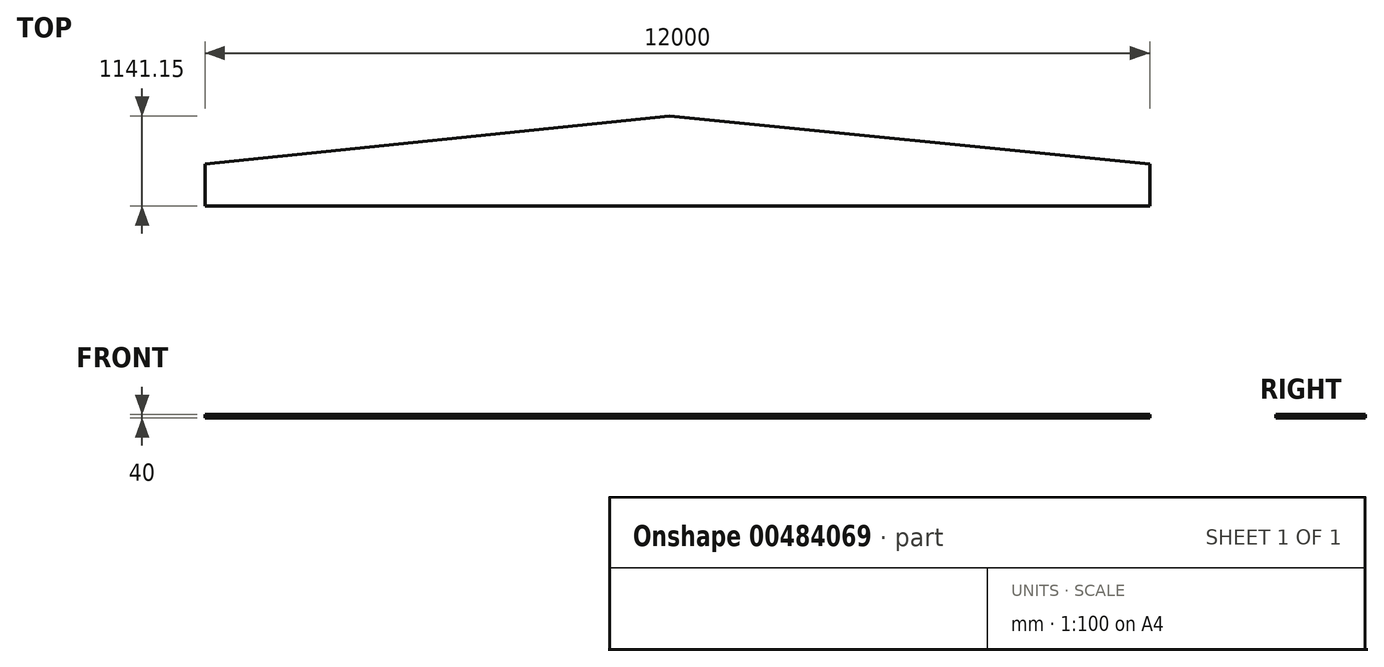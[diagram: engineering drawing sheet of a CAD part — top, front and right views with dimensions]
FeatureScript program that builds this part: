
annotation { "Feature Type Name" : "Feature", "Feature Type Description" : "" }
export const myFeature = defineFeature(function(context is Context, id is Id, definition is map)
    precondition{}
    {
        {
            var Q0;
            Q0=qCreatedBy(makeId("Top.planeOp"),FACE);
            var sketch = newSketch(context, id + "F0", { "sketchPlane" : qUnion([Q0])});
            skLineSegment(sketch, "E0", {"start": v(0, 0) * mm, "end": v(12000, 0) * mm});
            skLineSegment(sketch, "E1", {"start": v(6000, 0) * mm, "end": v(5899.43, 608.15) * mm});
            skLineSegment(sketch, "E2", {"start": v(5899.43, 608.15) * mm, "end": v(0, 0) * mm});
            skLineSegment(sketch, "E3", {"start": v(5899.43, 608.15) * mm, "end": v(12000, 0) * mm});
            skLineSegment(sketch, "E4.top", {"start": v(0, -533) * mm, "end": v(12000, -533) * mm});
            skLineSegment(sketch, "E4.left", {"start": v(0, 0) * mm, "end": v(0, -533) * mm});
            skLineSegment(sketch, "E4.right", {"start": v(12000, 0) * mm, "end": v(12000, -533) * mm});
            skSolve(sketch);
        }
        {
            var Q0;
            Q0=qSketchRegion(id+"F0",true);
            extrude(context, id + "F1", {"entities" : qUnion([Q0]), "depth" : 40 * mm, "offsetDistance" : 25 * mm});
        }
    });
